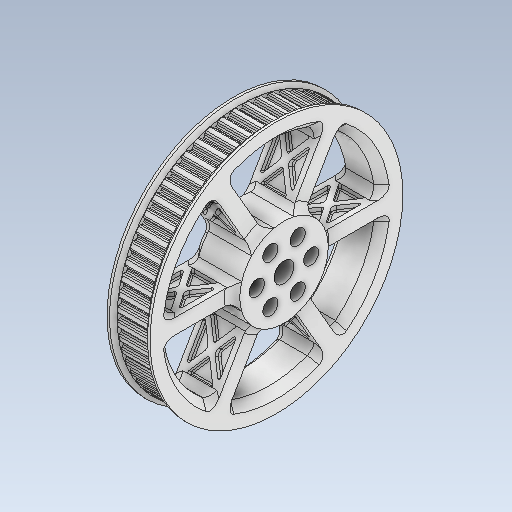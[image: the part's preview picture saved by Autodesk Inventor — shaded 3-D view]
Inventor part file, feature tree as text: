
AUTODESK INVENTOR PART (.ipt)
format: ipt  version: 2020 (Build 240168000, 168)  size: 3,581,952 bytes
history: native  units: mm
features: extrude x11, sketch x11, pattern_circular x8, fillet x7, thicken_offset x6, projected_geometry x6, chamfer x5, other x4, plane x2, reference x2
ambient origin geometry x8: Origin, YZ Plane, XZ Plane, XY Plane, X Axis, Y Axis, Z Axis, Center Point
bodies: Solid1 (feature_tree)
feature tree (62):
  plane  "Work Plane1"
  extrude  "Extrusion1"  Depth=110.0mm
  plane  "Work Plane2"
  extrude  "Extrusion2"  [1 undecoded]
  extrude  "Extrusion3"  Depth=20.0mm TaperAngle=0.0deg
  thicken_offset  "Thicken1"
  extrude  "Extrusion4"  Depth=10.0mm
  extrude  "Extrusion5"  Depth=20.0mm TaperAngle=0.0deg
  extrude  "Extrusion6"  Depth=3.0mm TaperAngle=0.0deg
  thicken_offset  "Thicken9"
  thicken_offset  "Thicken10"
  extrude  "Extrusion15"  Depth=1.0mm
  extrude  "Extrusion18"  Depth=1.0mm
  pattern_circular  "Circular Pattern2"  [2 undecoded]
  extrude  "Extrusion19"  Depth=0.5mm TaperAngle=0.0deg
  pattern_circular  "Circular Pattern3"  Count=6  [1 undecoded]
  fillet  "Fillet7"  Radius=93.0mm
  chamfer  "Chamfer8"  Distance=84.0mm
  fillet  "Fillet8"  Radius=6.0mm
  pattern_circular  "Circular Pattern4"  [2 undecoded]
  chamfer  "Chamfer9"  Distance=60.0mm
  fillet  "Fillet9"  [1 undecoded]
  pattern_circular  "Circular Pattern5"  [2 undecoded]
  chamfer  "Chamfer10"  Distance=26.0mm
  thicken_offset  "Thicken14"
  thicken_offset  "Thicken15"
  chamfer  "Chamfer11"  Distance=25.0mm
  chamfer  "Chamfer12"  Distance=60.0mm
  thicken_offset  "Thicken16"
  extrude  "Extrusion20"  Depth=0.5mm
  pattern_circular  "Circular Pattern6"  Angle=45.0deg  [1 undecoded]
  extrude  "Extrusion21"  Depth=0.5mm
  pattern_circular  "Circular Pattern7"  [2 undecoded]
  fillet  "Fillet10"  Radius=60.0mm
  fillet  "Fillet11"  Radius=2.0mm
  fillet  "Fillet12"  Radius=0.5mm
  pattern_circular  "Circular Pattern8"  [2 undecoded]
  fillet  "Fillet13"  Radius=1.5mm
  pattern_circular  "Circular Pattern9"  Angle=45.0deg  [1 undecoded]
  sketch  "Sketch1"  dims[d0=0.0mm d1=110.0mm]
  sketch  "Sketch2"  dims[d2=10.0mm d3=0.0mm d4=-1.0mm]
  sketch  "Sketch3"  dims[d5=110.0mm d6=20.0mm d7=0.0mm]
  projected_geometry  "Projected Loop1"
  sketch  "Sketch4"  dims[d8=20.0mm d9=0.0mm d10=10.0mm d11=9.0mm]
  projected_geometry  "Projected Loop2"
  sketch  "Sketch5"  dims[d12=8.0mm d13=20.0mm d14=0.0mm]
  sketch  "Sketch6"  dims[d15=102.0mm d16=3.0mm d17=0.0mm]
  sketch  "Sketch19"  dims[d18=3.0mm d19=0.0mm d143=1.0mm]
  projected_geometry  "Projected Loop15"
  sketch  "Sketch23"  dims[d144=1.0mm d145=1.0mm]
  reference  "Reference4"
  reference  "Reference5"
  sketch  "Sketch24"  dims[d146=1.0mm]
  projected_geometry  "Projected Loop17"
  sketch  "Sketch25"  dims[d164=35.0mm]
  projected_geometry  "Projected Loop18"
  sketch  "Sketch26"  dims[d165=3.0mm d166=0.0mm d176=6.0mm d177=25.0mm d178=0.0mm d179=60.0mm d180=62.831853mm d182=93.0mm d183=84.0mm d184=6.0mm d185=26.0mm d186=60.0mm d188=0.0mm d190=60.0deg d191=6.0mm d192=26.0mm d193=25.0mm d194=0.0mm d195=60.0mm d196=62.831853mm d198=3.0mm d199=3.0mm d200=2.0mm d201=45.0deg d202=3.0mm d203=60.0mm d204=62.831853mm d206=3.0mm d207=2.0mm d208=45.0deg d209=3.0mm d210=60.0mm d211=62.831853mm d213=1.0mm d214=2.0mm d215=45.0deg d216=0.5mm d217=1.0mm d218=0.5mm d219=1.0mm d220=1.5mm d221=2.0mm d222=45.0deg d223=1.5mm d224=2.0mm d225=45.0deg d226=0.05mm d227=0.05mm d228=0.0mm d229=2.0mm d230=13.0mm d231=2.0mm d232=2.0mm d233=2.0mm d234=0.0mm d235=60.0mm d236=360.0deg d238=2.0mm d239=0.0mm d240=60.0mm d241=360.0deg d243=0.5mm d244=0.5mm d245=2.0mm d246=60.0mm d247=62.831853mm d249=0.5mm d250=60.0mm d251=62.831853mm]
  projected_geometry  "Projected Loop19"
  other  "_ATP60XL037-A-C12_b"
  parser-record x1  (decoder bookkeeping rows leaked as tree rows — omitted from the tree; the rows remain in map.json)
  other  "xl_wheel_ass.iam"
  other  "xl_20_ori:1"
note: 15 required parameter values undecoded (feature->parameter linkage not recoverable at this tier; creation-order binding heuristic only, values carry confidence <= 0.55)
note: 1 file-system path scrubbed to <path> (originals preserved in map.json)
